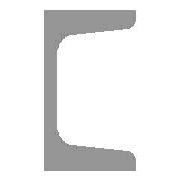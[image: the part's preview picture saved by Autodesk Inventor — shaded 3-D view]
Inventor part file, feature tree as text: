
AUTODESK INVENTOR PART (.ipt)
format: ipt  version: 2025 (Build 290162010, 162A)  size: 134,656 bytes
history: native  units: mm (DEFAULTED — no unit token found)
features: other x3, sketch x1, plane x1
ambient origin geometry x8: Origin, YZ Plane, XZ Plane, XY Plane, X Axis, Y Axis, Z Axis, Center Point
bodies: Solid1 (feature_tree), Body (feature_tree)
feature tree (5):
  other  "Driven Length"
  other  "Start plane"
  other  "End plane"
  sketch  "Sketch3"  dims[d0=5.0mm d1=50.0mm d2=50.0mm d3=7.5mm d4=22.5mm d5=1.968525mm d6=1500.0mm d7=0.0mm d23=8.0mm d24=4.0mm d25=15.4mm d26=-0.0mm d27=1500.0mm d28=90.0deg d29=1500.0mm]
  plane  "Work Plane3"
